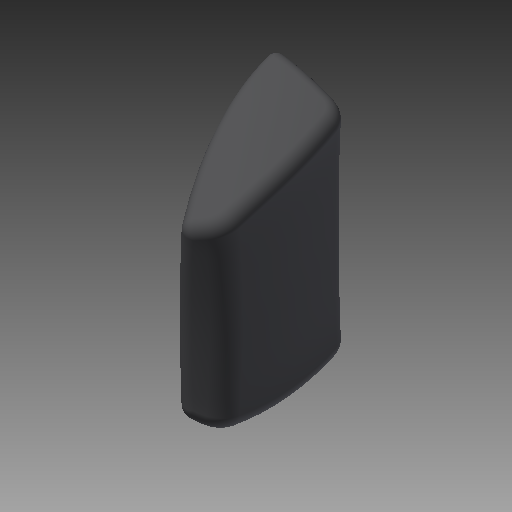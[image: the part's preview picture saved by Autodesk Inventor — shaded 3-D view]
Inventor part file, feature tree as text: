
AUTODESK INVENTOR PART (.ipt)
format: ipt  version: 2019 (Build 230136000, 136)  size: 2,187,776 bytes
history: native  units: mm
features: surface_op x34, sketch x14, other x9, fillet x8, sweep x5, plane x4, extrude x2, mirror x1, thicken_offset x1
ambient origin geometry x8: Origin, YZ Plane, XZ Plane, XY Plane, X Axis, Y Axis, Z Axis, Center Point
bodies: Solid1 (feature_tree)
feature tree (78):
  sketch  "Sketch1"  dims[d15=20.0mm d16=62.0mm d17=62.0mm d18=20.0mm d19=104.0mm]
  sketch  "Sketch2"  dims[d20=170.0mm d21=104.0mm]
  sketch  "Sketch3"  dims[d22=170.0mm d23=614.0mm]
  sketch  "Sketch5"  dims[d26=0.069mm d27=0.387465mm]
  sketch  "Sketch6"  dims[d28=2.298794mm d29=2.298794mm]
  sketch  "Sketch7"  dims[d30=16.0mm d31=16.0mm]
  sketch  "Sketch9"  dims[d32=0.0mm]
  plane  "Work Plane1"
  sketch  "Sketch10"  dims[d33=29.0mm]
  plane  "Work Plane2"
  sketch  "Sketch11"  dims[d34=29.0mm]
  sketch  "Sketch13"  dims[d36=72.0mm]
  plane  "Work Plane4"
  mirror  "Mirror1"
  surface_op  "Trim5"
  surface_op  "Extend1"
  surface_op  "Extend2"
  surface_op  "Trim7"
  surface_op  "Trim8"
  surface_op  "Trim9"
  surface_op  "Trim10"
  surface_op  "Trim11"
  surface_op  "Trim12"
  surface_op  "Trim13"
  surface_op  "Trim14"
  surface_op  "Extend3"
  surface_op  "Extend6"
  surface_op  "Extend7"
  surface_op  "Trim16"
  surface_op  "Trim17"
  surface_op  "Trim18"
  surface_op  "Extend4"
  surface_op  "Extend5"
  surface_op  "Trim19"
  surface_op  "Trim20"
  surface_op  "Trim21"
  surface_op  "Trim22"
  surface_op  "Trim26"
  surface_op  "Stitch Surface2"
  surface_op  "Trim27"
  surface_op  "Trim28"
  fillet  "Fillet6"  Radius=2.225295mm
  fillet  "Fillet7"  Radius=300.0mm
  fillet  "Fillet8"  [1 undecoded]
  fillet  "Fillet9"  [1 undecoded]
  surface_op  "Extend8"
  surface_op  "Extend9"
  surface_op  "Trim29"
  surface_op  "Trim30"
  surface_op  "Stitch Surface3"
  fillet  "Fillet10"  [1 undecoded]
  extrude  "Extrusion1"  Depth=62.0mm
  fillet  "Fillet12"  Radius=62.0mm
  fillet  "Fillet13"  Radius=20.0mm
  fillet  "Fillet14"  Radius=104.0mm
  thicken_offset  "Thicken2"
  sketch  "Sketch4"  dims[d24=0.069mm d25=0.387465mm]
  other  "Srf1"
  other  "Srf2"
  sketch  "Sketch12"  dims[d35=72.0mm]
  other  "Srf3"
  plane  "Work Plane3"
  other  "Srf4"
  sketch  "Sketch16"  dims[d37=111.5mm]
  other  "Srf5"
  other  "Srf6"
  other  "Srf8"
  sketch  "Sketch17"  dims[d38=111.5mm d39=162.0mm d40=162.0mm d41=2.0mm d42=2.0mm d43=10.5mm d44=10.5mm d45=26.0mm d46=26.0mm d47=70.0mm d48=70.0mm d49=718.25mm d50=-427.0mm d51=-232.75mm d100=0.0mm d101=192.25mm d102=52.0mm d103=92.0mm d104=134.25mm d105=170.0mm d106=52.0mm d107=92.0mm d108=134.25mm d109=170.0mm d110=0.5mm d111=3.0mm d112=8.7mm d113=18.3mm d114=0.5mm d115=3.0mm d116=8.7mm d117=18.3mm d118=0.0mm d119=30.0mm d120=30.0mm d121=19.0mm d122=45.0mm d123=45.0mm d124=23.5mm d125=23.5mm d156=30.0mm d157=15.0mm d158=35.0mm d159=10.0mm d160=18.25mm d161=19.0mm d162=15.0mm d163=93.0mm d164=46.0mm d165=192.0mm d167=96.0mm d168=25.0mm d169=13.0mm d170=13.0mm d171=5.0mm d172=0.0mm d174=5.0mm d179=1.5mm d180=1.5mm d181=5.0mm d182=5.0mm d183=0.254mm d184=0.254mm d185=0.0mm d186=0.0mm d187=0.0mm d188=0.0mm]
  extrude  "ExtrusionSrf1"  Depth=104.0mm
  sweep  "SweepSrf4"
  sweep  "SweepSrf5"
  sweep  "SweepSrf6"
  sweep  "SweepSrf7"
  surface_op  "Surface2"
  surface_op  "Surface3"
  sweep  "SweepSrf8"
  other  "Srf7"
  other  "Srf9"
note: 3 required parameter values undecoded (feature->parameter linkage not recoverable at this tier; creation-order binding heuristic only, values carry confidence <= 0.55)
